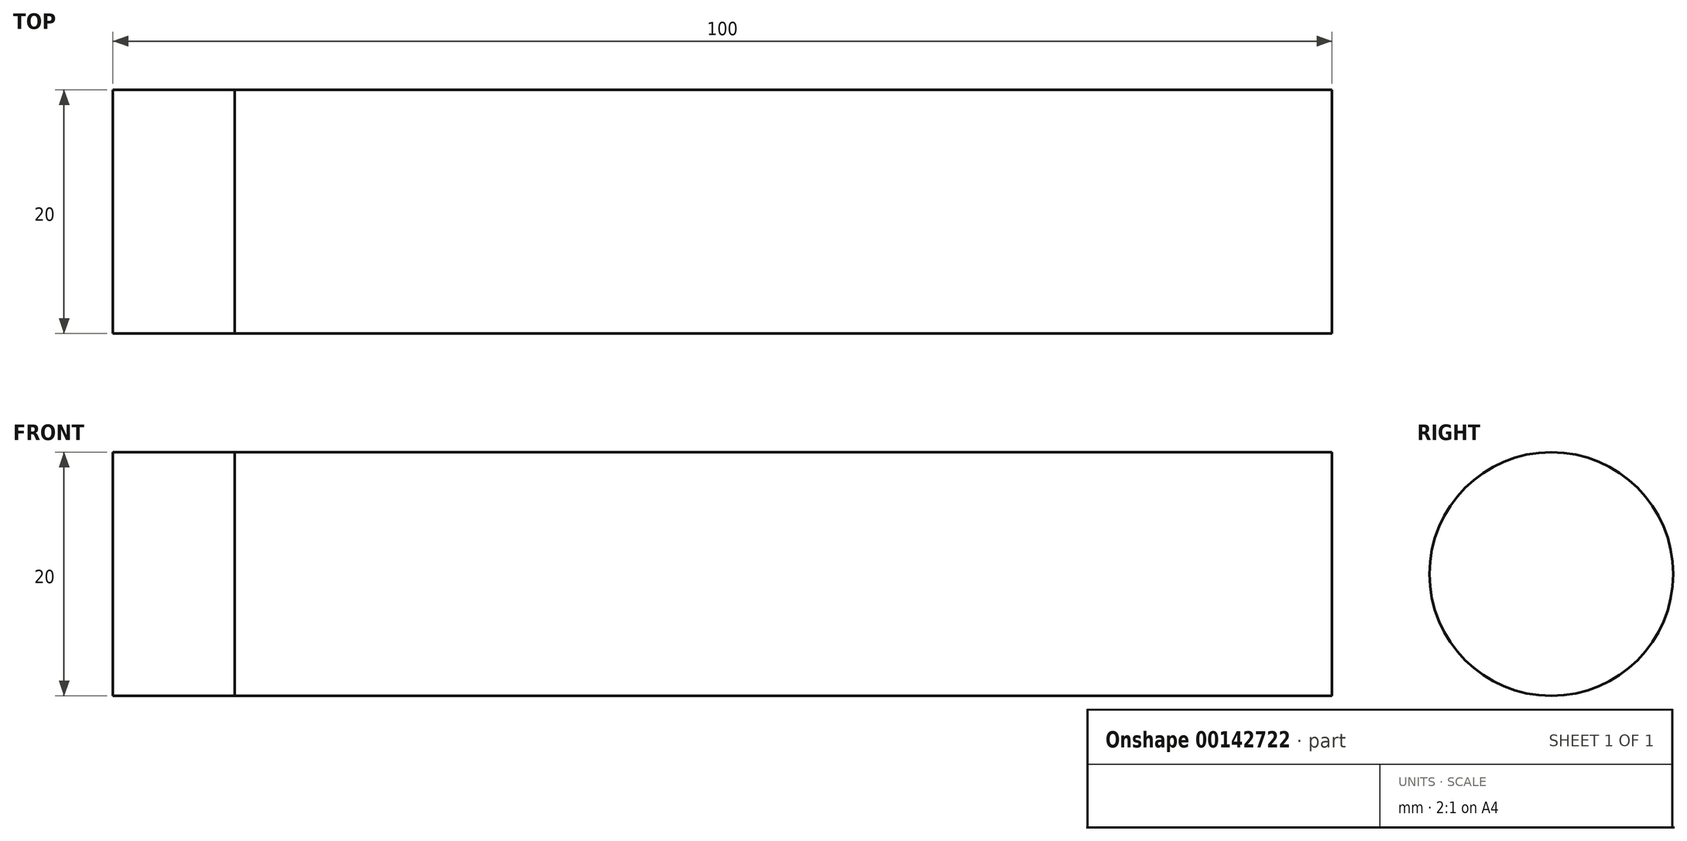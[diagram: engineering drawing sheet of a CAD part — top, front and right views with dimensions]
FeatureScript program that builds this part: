
annotation { "Feature Type Name" : "Feature", "Feature Type Description" : "" }
export const myFeature = defineFeature(function(context is Context, id is Id, definition is map)
    precondition{}
    {
        {
            var Q0;
            Q0=qCreatedBy(makeId("Right.planeOp"),FACE);
            var sketch = newSketch(context, id + "F0", { "sketchPlane" : qUnion([Q0])});
            skCircle(sketch, "E0", {"center": v(0, 0) * mm, "radius": 10 * mm});
            skSolve(sketch);
        }
        {
            var Q0;
            Q0 = qSketchRegion(id + "F0", true);
            extrude(context, id + "F1", {"entities" : qUnion([Q0]), "depth" : 10 * mm});
        }
        {
            var Q0;
            Q0=makeQuery(id+"F1.opExtrude","CAP_FACE",FACE,{"disambiguationData":[OSD([sQuery(id+"F0.wireOp",EDGE,"E0")])],"isStart":false});
            var sketch = newSketch(context, id + "F2", { "sketchPlane" : qUnion([Q0])});
            skCircle(sketch, "E1", {"center": v(0, 0) * mm, "radius": 10 * mm});
            skSolve(sketch);
        }
        {
            var Q0;
            Q0 = qSketchRegion(id + "F2", true);
            extrude(context, id + "F3", {"entities" : qUnion([Q0]), "depth" : 90 * mm});
        }
    });
